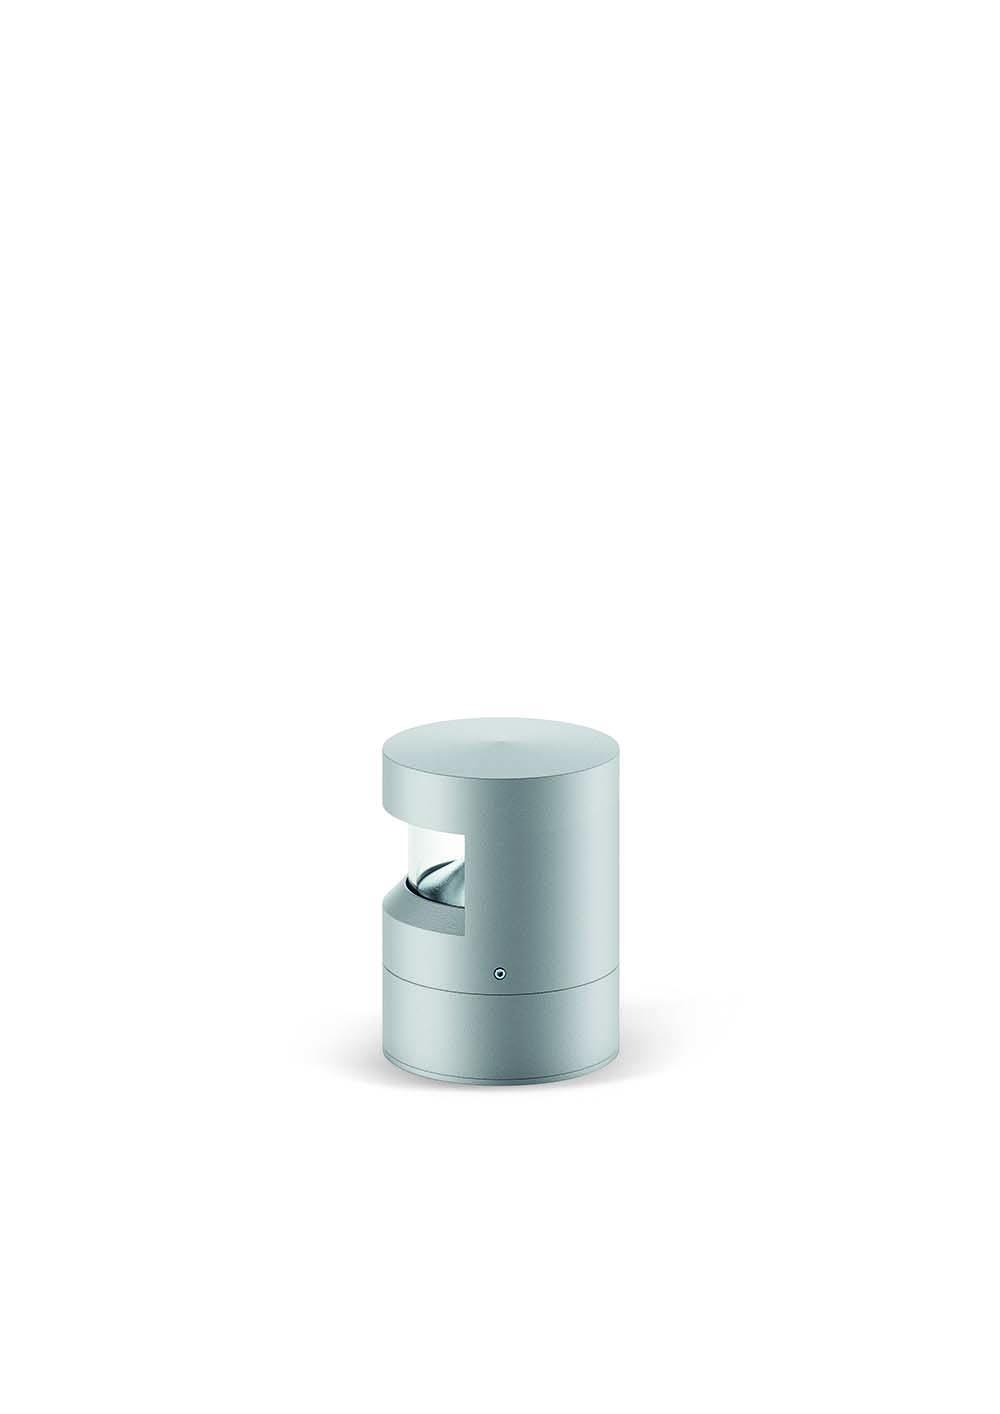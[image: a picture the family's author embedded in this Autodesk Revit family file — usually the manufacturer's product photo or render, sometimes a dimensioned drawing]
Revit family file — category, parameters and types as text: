
# Revit family: Platek_Mirco Menhir_1_Opening
name_source: partatom
category: Apparecchi per illuminazione
revit_build: Autodesk Revit 2017 (Build: 20160225_1515(x64)
units: mm (PartAtom-declared; Revit-internal decimal feet)

## family parameters
Basato su piano di lavoro = Sì
Condiviso = Sì
Punto di calcolo locali = No
Quota connettore circolare = Usa diametro
Sempre verticale = No
Sorgente d'illuminazione = Sì
Taglio con vuoti quando caricato = No
Tipo di parte = Normale

## types (3) — shared parameters
Angolo inclinazione = 90.00°
Beam Angle = 0.00°
Body = PLK_Grey
CRI = >80
Carico apparente = 0 VA
Colour Temperature = 3000 K
Commenti sul tipo = Pedestrian areas, Urban zones, Paths, Roads
Descrizione = Outdoor Lighting, Floor/Ground Illumination
Diffuse Type = PMMA
Dimmable = Yes
Emetti da diametro cerchio = 10 mm  [stored 0.0328084 ft]
Energy Efficiency Rating = A/A+/A++
Filtro dei colori = 16777215
Frequency = 50/60 Hz
IK Rating = IK08
IP Rating = IP65
Insulation Class = 2
LED Protection = Surge protection included
Lampada = LED
Light Source = PLK_Light Source
Modello = MICRO MENHIR
Mounting Type = Ground
Nota chiave = Other Led colors available on request, IP68 connector included
PLATEK FInishes = Painted Aluminium Avalaible in Anthracite/Black/White/Corten/Bronze
Power Supply Unit = Included
Product Documentation Link = http://www.platek.eu
Product Page URL = http://www.platek.eu
Produttore = PLATEK SRL
Prospetto di default = 1219.2 mm  [stored 4 ft]
Rendi la forma visibile nel rendering = No
Supply Voltage = 230 V
Supply Voltage Max = 240 V
Supply Voltage Min = 220 V
URL = www.platek.eu
Variazione temperatura colore lampada con luminosità attenuata = <Nessuno>

## per-type parameters (varying)
| type | Aluminium | Codice assieme | File diagramma fotometrico | Height | Height150 | Height500 | Height800 | Immagine tipo | Luminaire Luminous Flux | Luminaire Luminous Intensity | Luminaire Wattage | Manufacturer Comment | PLATEK Article Code | Product Dimension |
| 4011111_9,6W_LED_3000K_H150mm | PLK_Aluminium | 4011111.06(Grey); 4011111.08(Anthracite); 4011111.01(Black); 4011111.02(White); 4011111.07(Corten); 4011111.09(Bronze) | 4011111.IES | 43 mm  [stored 0.141076 ft] | Sì | No | No | micro_menhir_15_02.jpg | 255 lm | 203 cd | 10 W | 4mmThick PMMA | 4011111 | D115mm x H150mm |
| 4011211_13,5W_LED_3000K_H500mm | PLK_Light Source | 4011211.06(Grey); 4011211.08(Anthracite); 4011211.01(Black); 4011211.02(White); 4011211.07(Corten); 4011211.09(Bronze) | 4011211.IES | 403 mm  [stored 1.32218 ft] | No | Sì | No | micro_menhir_50_1 finestra.jpg | 340 lm | 283 cd | 14 W | 4mm Thick PMMA | 4011211 | D115mm x H500mm |
| 4011311_13,5W_LED_3000K_H800mm | PLK_Aluminium | 4011311.06(Grey); 4011311.08(Anthracite); 4011311.01(Black); 4011311.02(White); 4011311.07(Corten); 4011311.09(Bronze) | 4011311.IES | 703 mm  [stored 2.30643 ft] | No | No | Sì | micro_menhir_80.jpg | 340 lm | 283 cd | 14 W | 4mm Thick PMMA | 4011311 | D115mm x H800mm |

note: [stored X ft] marks values corroborated as IEEE doubles in the binary element streams (Revit-internal decimal feet)
